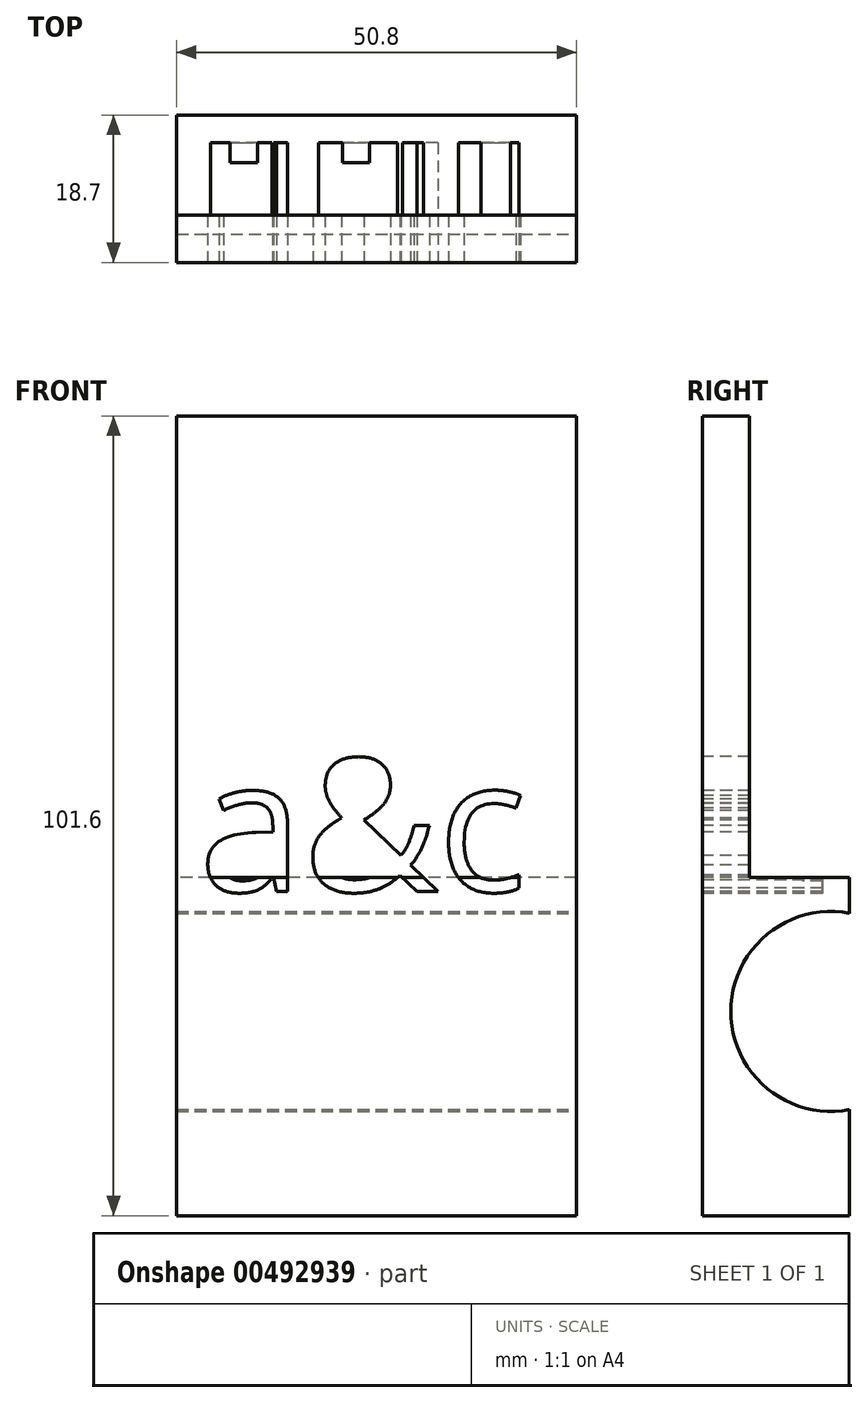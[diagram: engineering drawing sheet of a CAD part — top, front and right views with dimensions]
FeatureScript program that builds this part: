
annotation { "Feature Type Name" : "Feature", "Feature Type Description" : "" }
export const myFeature = defineFeature(function(context is Context, id is Id, definition is map)
    precondition{}
    {
        {
            var Q0;
            Q0=qCreatedBy(makeId("Front.planeOp"),FACE);
            var sketch = newSketch(context, id + "F0", { "sketchPlane" : qUnion([Q0])});
            skLineSegment(sketch, "E0.bottom", {"start": v(-50.8, 103.86) * mm, "end": v(0, 103.86) * mm});
            skLineSegment(sketch, "E0.top", {"start": v(-50.8, 2.26) * mm, "end": v(0, 2.26) * mm});
            skLineSegment(sketch, "E0.left", {"start": v(-50.8, 103.86) * mm, "end": v(-50.8, 2.26) * mm});
            skLineSegment(sketch, "E0.right", {"start": v(0, 103.86) * mm, "end": v(0, 2.26) * mm});
            skSolve(sketch);
        }
        {
            var Q0;
            Q0=makeQuery(id+"F0.imprint","IMPRINT",FACE,{"disambiguationData":[TD([[makeQuery(id+"F0.imprint","IMPRINT",EDGE,{"derivedFrom":sQuery(id+"F0.wireOp",EDGE,"E0.bottom")}),-1.0]])]});
            extrude(context, id + "F1", {"entities" : qUnion([Q0]), "depth" : 6 * mm, "offsetDistance" : 25.4 * mm});
        }
        {
            var Q0;
            Q0=makeQuery(id+"F1.opExtrude","SWEPT_FACE",FACE,{"disambiguationData":[OSD([sQuery(id+"F0.wireOp",EDGE,"E0.right")])]});
            var sketch = newSketch(context, id + "F2", { "sketchPlane" : qUnion([Q0])});
            skCircle(sketch, "E1", {"center": v(-2.61, 95.94) * mm, "radius": 2.5 * mm});
            skSolve(sketch);
        }
        {
            var Q0;
            Q0 = qSketchRegion(id + "F2", true);
            extrude(context, id + "F3", {"entities" : qUnion([Q0]), "operationType" : NewBodyOperationType.REMOVE, "endBound" : BoundingType.THROUGH_ALL, "oppositeDirection" : true, "depth" : 25.4 * mm, "offsetDistance" : 25.4 * mm});
        }
        {
            var Q0;
            {var subQ0=sQuery(id+"F0.wireOp",EDGE,"E0.top");var subQ1=sQuery(id+"F0.wireOp",EDGE,"E0.left");var subQ2=sQuery(id+"F0.wireOp",EDGE,"E0.right");Q0=makeQuery(id+"F3.boolean.opBoolean","SPLIT",FACE,{"disambiguationData":[TD([makeQuery(id+"F1.opExtrude","SWEPT_FACE",FACE,{"disambiguationData":[OSD([subQ0])]})])],"derivedFrom":makeQuery(id+"F1.opExtrude","CAP_FACE",FACE,{"disambiguationData":[OSD([sQuery(id+"F0.wireOp",EDGE,"E0.bottom"),subQ0,subQ1,subQ2])],"isStart":false})});}
            var sketch = newSketch(context, id + "F4", { "sketchPlane" : qUnion([Q0])});
            skText(sketch, "E2", { "text": "a&c\n", "fontName": "OpenSans-Regular.ttf"});
            const initialGuessF4  = {"E2": [-0.04792, 0.04345, 1, 0, 0.01699]};
            skSetInitialGuess(sketch, initialGuessF4);
            skSolve(sketch);
        }
        {
            var Q0;
            Q0 = qSketchRegion(id + "F4", true);
            extrude(context, id + "F5", {"entities" : qUnion([Q0]), "operationType" : NewBodyOperationType.REMOVE, "oppositeDirection" : true, "depth" : 2.54 * mm, "offsetDistance" : 25.4 * mm});
        }
        {
            var Q0;
            Q0=makeQuery(id+"F1.opExtrude","CAP_FACE",FACE,{"disambiguationData":[OSD([sQuery(id+"F0.wireOp",EDGE,"E0.bottom"),sQuery(id+"F0.wireOp",EDGE,"E0.top"),sQuery(id+"F0.wireOp",EDGE,"E0.left"),sQuery(id+"F0.wireOp",EDGE,"E0.right")])],"isStart":true});
            var sketch = newSketch(context, id + "F6", { "sketchPlane" : qUnion([Q0])});
            skLineSegment(sketch, "E3.bottom", {"start": v(0, 45.2) * mm, "end": v(50.8, 45.2) * mm});
            skLineSegment(sketch, "E3.top", {"start": v(0, 2.26) * mm, "end": v(50.8, 2.26) * mm});
            skLineSegment(sketch, "E3.left", {"start": v(0, 45.2) * mm, "end": v(0, 2.26) * mm});
            skLineSegment(sketch, "E3.right", {"start": v(50.8, 45.2) * mm, "end": v(50.8, 2.26) * mm});
            skSolve(sketch);
        }
        {
            var Q0;
            {var subQ0=sQuery(id+"F0.wireOp",EDGE,"E0.top");var subQ1=sQuery(id+"F0.wireOp",EDGE,"E0.bottom");var subQ2=sQuery(id+"F0.wireOp",EDGE,"E0.left");var subQ3=sQuery(id+"F0.wireOp",EDGE,"E0.right");Q0=makeQuery(id+"F5.boolean.opBoolean","SPLIT",FACE,{"disambiguationData":[TD([makeQuery(id+"F1.opExtrude","SWEPT_FACE",FACE,{"disambiguationData":[OSD([subQ1])]})])],"derivedFrom":makeQuery(id+"F1.opExtrude","CAP_FACE",FACE,{"disambiguationData":[OSD([subQ1,subQ0,subQ2,subQ3])],"isStart":false})});}
            extrude(context, id + "F7", {"entities" : qUnion([Q0]), "operationType" : NewBodyOperationType.ADD, "depth" : 12.7 * mm, "offsetDistance" : 25.4 * mm});
        }
        {
            var Q0;
            {var subQ0=sQuery(id+"F6.wireOp",EDGE,"E3.bottom");Q0=makeQuery(id+"F6.imprint","IMPRINT",FACE,{"disambiguationData":[TD([[makeQuery(id+"F6.imprint","IMPRINT",EDGE,{"derivedFrom":subQ0}),1.0]])]});}
            extrude(context, id + "F8", {"entities" : qUnion([Q0]), "operationType" : NewBodyOperationType.REMOVE, "oppositeDirection" : true, "depth" : 12.7 * mm, "offsetDistance" : 25.4 * mm});
        }
        {
            var Q0;
            {var subQ0=sQuery(id+"F0.wireOp",EDGE,"E0.right");Q0=makeQuery(id+"F7.boolean.opBoolean","MERGE",FACE,{"derivedFrom":[makeQuery(id+"F1.opExtrude","SWEPT_FACE",FACE,{"disambiguationData":[OSD([subQ0])]}),makeQuery(id+"F7.opExtrude","SWEPT_FACE",FACE,{"disambiguationData":[OSD([subQ0])]})]});}
            var sketch = newSketch(context, id + "F9", { "sketchPlane" : qUnion([Q0])});
            skCircle(sketch, "E4", {"center": v(-2.4, 28.2) * mm, "radius": 12.7 * mm});
            skSolve(sketch);
        }
        {
            var Q0;
            Q0 = qSketchRegion(id + "F9", true);
            extrude(context, id + "F10", {"entities" : qUnion([Q0]), "operationType" : NewBodyOperationType.REMOVE, "endBound" : BoundingType.THROUGH_ALL, "oppositeDirection" : true, "depth" : 25.4 * mm, "offsetDistance" : 25.4 * mm});
        }
    });
